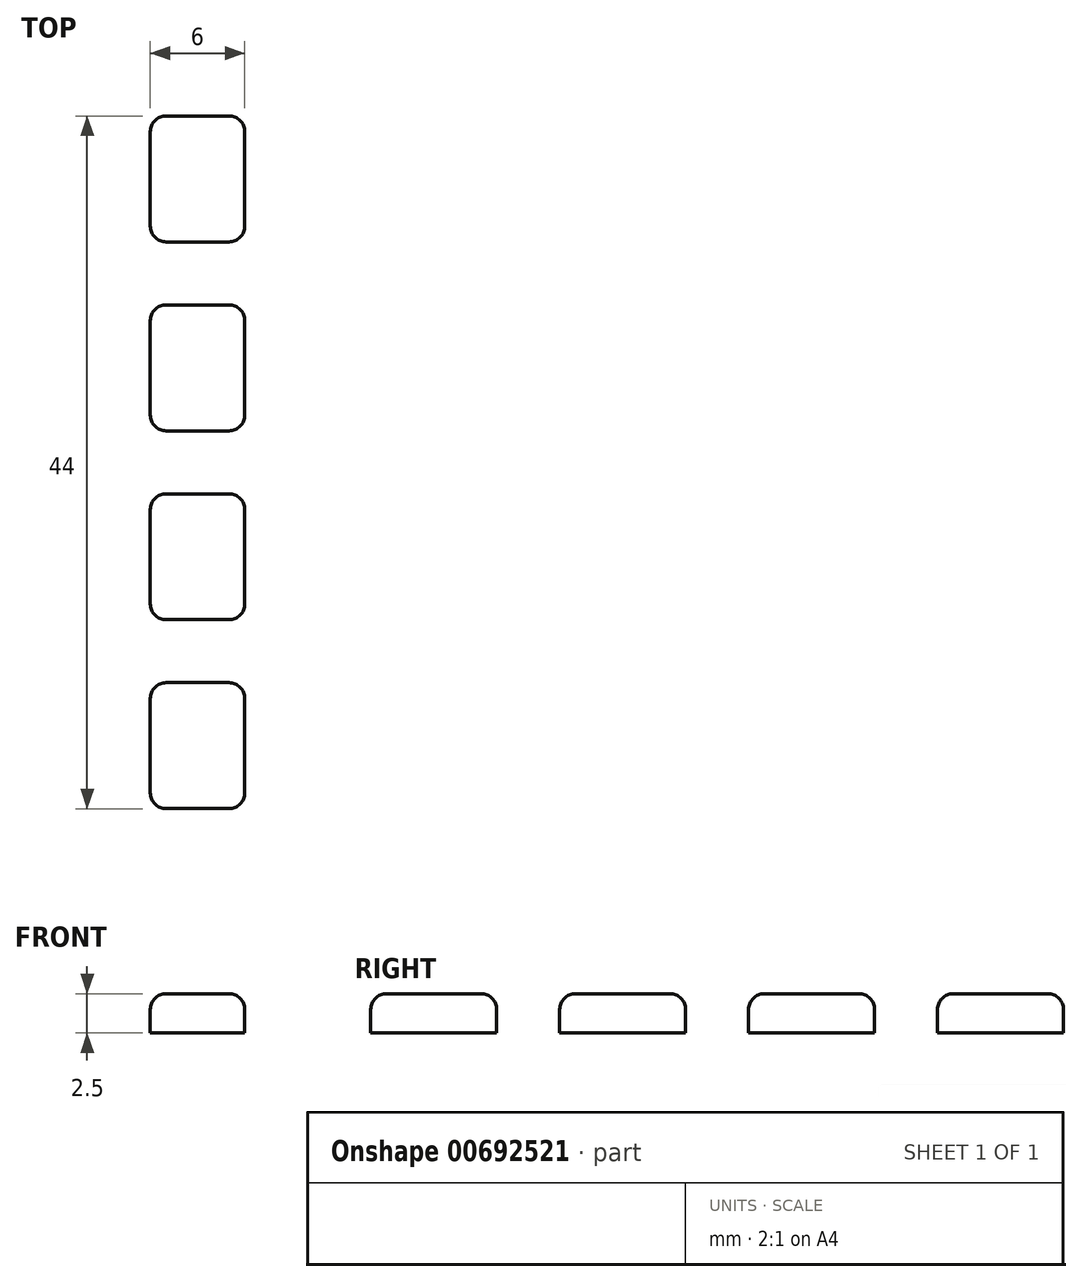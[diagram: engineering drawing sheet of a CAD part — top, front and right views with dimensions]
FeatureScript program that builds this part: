
annotation { "Feature Type Name" : "Feature", "Feature Type Description" : "" }
export const myFeature = defineFeature(function(context is Context, id is Id, definition is map)
    precondition{}
    {
        {
            var Q0;
            Q0=qCreatedBy(makeId("Top.planeOp"),FACE);
            var sketch = newSketch(context, id + "F0", { "sketchPlane" : qUnion([Q0])});
            skLineSegment(sketch, "E0.bottom", {"start": v(-5, 40.6) * mm, "end": v(-1, 40.6) * mm});
            skLineSegment(sketch, "E0.top", {"start": v(-5, 32.6) * mm, "end": v(-1, 32.6) * mm});
            skLineSegment(sketch, "E0.left", {"start": v(-6, 39.6) * mm, "end": v(-6, 33.6) * mm});
            skLineSegment(sketch, "E0.right", {"start": v(0, 39.6) * mm, "end": v(0, 33.6) * mm});
            skPoint(sketch, "E1.visualSharp", {"position": v(-6, 40.6) * mm});
            skArc(sketch, "E1.filletArc", {"start": v(-5, 40.6) * mm, "mid": v(-5.7, 40.31) * mm, "end": v(-6, 39.6) * mm});
            skPoint(sketch, "E2.visualSharp", {"position": v(-6, 32.6) * mm});
            skArc(sketch, "E2.filletArc", {"start": v(-6, 33.6) * mm, "mid": v(-5.7, 32.9) * mm, "end": v(-5, 32.6) * mm});
            skPoint(sketch, "E3.visualSharp", {"position": v(0, 32.6) * mm});
            skArc(sketch, "E3.filletArc", {"start": v(-1, 32.6) * mm, "mid": v(-0.3, 32.9) * mm, "end": v(0, 33.6) * mm});
            skPoint(sketch, "E4.visualSharp", {"position": v(0, 40.6) * mm});
            skArc(sketch, "E4.filletArc", {"start": v(0, 39.6) * mm, "mid": v(-0.3, 40.31) * mm, "end": v(-1, 40.6) * mm});
            skLineSegment(sketch, "E5.bottom", {"start": v(-5, 28.6) * mm, "end": v(-1, 28.6) * mm});
            skLineSegment(sketch, "E5.top", {"start": v(-5, 20.6) * mm, "end": v(-1, 20.6) * mm});
            skLineSegment(sketch, "E5.left", {"start": v(-6, 27.6) * mm, "end": v(-6, 21.6) * mm});
            skLineSegment(sketch, "E5.right", {"start": v(0, 27.6) * mm, "end": v(0, 21.6) * mm});
            skPoint(sketch, "E6.visualSharp", {"position": v(-6, 28.6) * mm});
            skArc(sketch, "E6.filletArc", {"start": v(-5, 28.6) * mm, "mid": v(-5.7, 28.31) * mm, "end": v(-6, 27.6) * mm});
            skPoint(sketch, "E7.visualSharp", {"position": v(-6, 20.6) * mm});
            skArc(sketch, "E7.filletArc", {"start": v(-6, 21.6) * mm, "mid": v(-5.7, 20.9) * mm, "end": v(-5, 20.6) * mm});
            skPoint(sketch, "E8.visualSharp", {"position": v(0, 20.6) * mm});
            skArc(sketch, "E8.filletArc", {"start": v(-1, 20.6) * mm, "mid": v(-0.3, 20.9) * mm, "end": v(0, 21.6) * mm});
            skPoint(sketch, "E9.visualSharp", {"position": v(0, 28.6) * mm});
            skArc(sketch, "E9.filletArc", {"start": v(0, 27.6) * mm, "mid": v(-0.3, 28.31) * mm, "end": v(-1, 28.6) * mm});
            skLineSegment(sketch, "E10.bottom", {"start": v(-5, 16.6) * mm, "end": v(-1, 16.6) * mm});
            skLineSegment(sketch, "E10.top", {"start": v(-5, 8.6) * mm, "end": v(-1, 8.6) * mm});
            skLineSegment(sketch, "E10.left", {"start": v(-6, 15.6) * mm, "end": v(-6, 9.6) * mm});
            skLineSegment(sketch, "E10.right", {"start": v(0, 15.6) * mm, "end": v(0, 9.6) * mm});
            skPoint(sketch, "E11.visualSharp", {"position": v(-6, 16.6) * mm});
            skArc(sketch, "E11.filletArc", {"start": v(-5, 16.6) * mm, "mid": v(-5.7, 16.31) * mm, "end": v(-6, 15.6) * mm});
            skPoint(sketch, "E12.visualSharp", {"position": v(-6, 8.6) * mm});
            skArc(sketch, "E12.filletArc", {"start": v(-6, 9.6) * mm, "mid": v(-5.7, 8.9) * mm, "end": v(-5, 8.6) * mm});
            skPoint(sketch, "E13.visualSharp", {"position": v(0, 8.6) * mm});
            skArc(sketch, "E13.filletArc", {"start": v(-1, 8.6) * mm, "mid": v(-0.3, 8.9) * mm, "end": v(0, 9.6) * mm});
            skPoint(sketch, "E14.visualSharp", {"position": v(0, 16.6) * mm});
            skArc(sketch, "E14.filletArc", {"start": v(0, 15.6) * mm, "mid": v(-0.3, 16.31) * mm, "end": v(-1, 16.6) * mm});
            skLineSegment(sketch, "E15.bottom", {"start": v(-5, 4.6) * mm, "end": v(-1, 4.6) * mm});
            skLineSegment(sketch, "E15.top", {"start": v(-5, -3.4) * mm, "end": v(-1, -3.4) * mm});
            skLineSegment(sketch, "E15.left", {"start": v(-6, 3.6) * mm, "end": v(-6, -2.4) * mm});
            skLineSegment(sketch, "E15.right", {"start": v(0, 3.6) * mm, "end": v(0, -2.4) * mm});
            skPoint(sketch, "E16.visualSharp", {"position": v(-6, 4.6) * mm});
            skArc(sketch, "E16.filletArc", {"start": v(-5, 4.6) * mm, "mid": v(-5.7, 4.31) * mm, "end": v(-6, 3.6) * mm});
            skPoint(sketch, "E17.visualSharp", {"position": v(-6, -3.4) * mm});
            skArc(sketch, "E17.filletArc", {"start": v(-6, -2.4) * mm, "mid": v(-5.7, -3.1) * mm, "end": v(-5, -3.4) * mm});
            skPoint(sketch, "E18.visualSharp", {"position": v(0, -3.4) * mm});
            skArc(sketch, "E18.filletArc", {"start": v(-1, -3.4) * mm, "mid": v(-0.3, -3.1) * mm, "end": v(0, -2.4) * mm});
            skPoint(sketch, "E19.visualSharp", {"position": v(0, 4.6) * mm});
            skArc(sketch, "E19.filletArc", {"start": v(0, 3.6) * mm, "mid": v(-0.3, 4.31) * mm, "end": v(-1, 4.6) * mm});
            skSolve(sketch);
        }
        {
            var Q0;
            Q0 = qSketchRegion(id + "F0", true);
            extrude(context, id + "F1", {"entities" : qUnion([Q0]), "depth" : 2.5 * mm, "offsetDistance" : 25 * mm});
        }
        {
            var Q0;
            Q0=makeQuery(id+"F1.opExtrude","CAP_FACE",FACE,{"disambiguationData":[OSD([sQuery(id+"F0.wireOp",EDGE,"E0.bottom"),sQuery(id+"F0.wireOp",EDGE,"E0.top"),sQuery(id+"F0.wireOp",EDGE,"E0.left"),sQuery(id+"F0.wireOp",EDGE,"E0.right"),sQuery(id+"F0.wireOp",EDGE,"E1.filletArc"),sQuery(id+"F0.wireOp",EDGE,"E2.filletArc"),sQuery(id+"F0.wireOp",EDGE,"E3.filletArc"),sQuery(id+"F0.wireOp",EDGE,"E4.filletArc")])],"isStart":false});
            var Q1;
            Q1=makeQuery(id+"F1.opExtrude","CAP_FACE",FACE,{"disambiguationData":[OSD([sQuery(id+"F0.wireOp",EDGE,"E5.bottom"),sQuery(id+"F0.wireOp",EDGE,"E5.top"),sQuery(id+"F0.wireOp",EDGE,"E5.left"),sQuery(id+"F0.wireOp",EDGE,"E5.right"),sQuery(id+"F0.wireOp",EDGE,"E6.filletArc"),sQuery(id+"F0.wireOp",EDGE,"E7.filletArc"),sQuery(id+"F0.wireOp",EDGE,"E8.filletArc"),sQuery(id+"F0.wireOp",EDGE,"E9.filletArc")])],"isStart":false});
            var Q2;
            Q2=makeQuery(id+"F1.opExtrude","CAP_FACE",FACE,{"disambiguationData":[OSD([sQuery(id+"F0.wireOp",EDGE,"E10.bottom"),sQuery(id+"F0.wireOp",EDGE,"E10.top"),sQuery(id+"F0.wireOp",EDGE,"E10.left"),sQuery(id+"F0.wireOp",EDGE,"E10.right"),sQuery(id+"F0.wireOp",EDGE,"E11.filletArc"),sQuery(id+"F0.wireOp",EDGE,"E12.filletArc"),sQuery(id+"F0.wireOp",EDGE,"E13.filletArc"),sQuery(id+"F0.wireOp",EDGE,"E14.filletArc")])],"isStart":false});
            var Q3;
            Q3=makeQuery(id+"F1.opExtrude","CAP_FACE",FACE,{"disambiguationData":[OSD([sQuery(id+"F0.wireOp",EDGE,"E15.bottom"),sQuery(id+"F0.wireOp",EDGE,"E15.top"),sQuery(id+"F0.wireOp",EDGE,"E15.left"),sQuery(id+"F0.wireOp",EDGE,"E15.right"),sQuery(id+"F0.wireOp",EDGE,"E16.filletArc"),sQuery(id+"F0.wireOp",EDGE,"E17.filletArc"),sQuery(id+"F0.wireOp",EDGE,"E18.filletArc"),sQuery(id+"F0.wireOp",EDGE,"E19.filletArc")])],"isStart":false});
            fillet(context, id + "F2", {"entities" : qUnion([Q0, Q1, Q2, Q3]), "radius" : 1 * mm, "tangentPropagation" : true, "allowEdgeOverflow" : false});
        }
    });
